# Revit family: Electronics_Loudspeaker_Bose-Professional_Designmax_DM2S
name_source: partatom
category: Communication Devices
revit_build: Autodesk Revit 2017 (Build: 20190508_0315(x64)
units: mm (PartAtom-declared; Revit-internal decimal feet)

## family parameters
Cut with Voids When Loaded = No
Host = Face
Maintain Annotation Orientation = No
OmniClass Number = 23.85.10.11.14.14.14
OmniClass Title = Loudspeakers
Part Type = Normal
Room Calculation Point = No
Round Connector Dimension = Use Diameter
Shared = No

## types (2) — shared parameters
Assembly Code = D5030
Bracket Material = Metal-Bose-Aluminium
Default Elevation = 1219 mm
Depth = 116 mm
Description = Premium sound to maximize any design.
DesignMax loudspeakers bring outstanding audio and aesthetics to any commercial space. With 12 models to choose from, it’s easy to create tailored solutions that deliver instantly impressive sound. QuickHold mounting mechanisms make installation efficient, reducing strain and hassle — and saving substantial time. And with both black and white versions available, DesignMax loudspeakers integrate seamlessly with any décor.

Ideal for background music, the 16-watt DesignMax DM2S loudspeaker features a 2.25-inch transducer and 80 Hz - 19 kHz frequency range. The DM2S is surface-mounted and locks onto a hidden QuickHold U-bracket for fast, secure installation.

FEATURES
Combine models to complete any design, big or small — 12 loudspeakers to mix and match, from 2-inch, low-profile models to 8-inch, high-SPL compression-driver loudspeakers and outdoor-rated options

Deliver instantly impressive sound with custom Bose drivers — no DSP or EQ required. For even better sound, use select Bose DSPs and amplifiers to enable Bose loudspeaker EQ and SmartBass processing, which expands performance and response at any listening level.

Blend with any room design with elegant form factor, minimum-bezel grilles available in black or white, and removable logos

Reduce installation time with the patented QuickHold mounting system, which also reduces strain, hassle, and the chance of product damage

Install easily — all models include Euroblock connectors; ceiling-mounted models include plenum-rated backcans, tile-bridges, and front-access audio wiring that makes installation and troubleshooting easier

Applications
Performing arts venues
Places of worship
Conference centers
Retail stores
Restaurants and bars
Hospitality venues
Edition number = 1
Environmental = indoor only
Frequency Range = 85 – 19,000 Hz
Frequency Response = 95 – 18,000 Hz
Full-Range Driver = 1 x 2.25-inch woofer (57 mm)
Height = 182 mm
Keynote = 16700
Manufacturer = Bose Professional
Model = DesignMax DM2S
Mounting/Suspension = QuickHold Mounting system with included U-Bracket
Nominal Coverage Pattern = 160° x 135°
Nominal Impedance = 16 Ω  (transformer bypass)
Nominal Sensitivity = 82 dB
Operating Temperature Range = 0 to 50 °C (32 °F to 122 °F)
Power Connector = Euroblock 6-pin connector with loop-through, front-baffle mounted. Accepts 18 AWG (0.8 mm2) to 14 AWG (2.5 mm2) size wire
Power Handling(Long-term continuous) = 16W
Power Handling(peak) = 64W
Product Guid = 9e5f6eb0-d35b-432c-9cf5-732f3da14a42
Product data url = https://www.bimobject.com
Rated Maximum SPL = 94 dB
Recommended High-pass Filter = 85 Hz with recommended 24 dB / octave filter
Safety Agency = UL-1480A, S5591/ UL Listed, NFPA70, in accordance with IEC60268-5, ROHS, CE compliant
Transformer Taps Information = 70V: 1.2, 2.3, 4.5, 9 W, bypass, 100V: 2.3, 4.5, 9 W, bypass
URL = https://www.bose.com
Weight = 1.32 kg
Width = 113 mm
Wire/ Conduit Entry = Accepts 18 AWG (0.8 mm2) to 14 AWG (2.5 mm2) size wire

## per-type parameters (varying)
| type | Mesh Material | Product code | Speaker Material |
| DM2S-White | Grill-Bose-White | 815011-0210 | Metal-Bose-White |
| DM2S-Black | Grill-Bose-Black | 815011-0110 | Metal-Bose-Black |

## geometry (parser evidence)
native form markers: Blend x4, Sweep x8
no freeform markers — native parametric forms only
